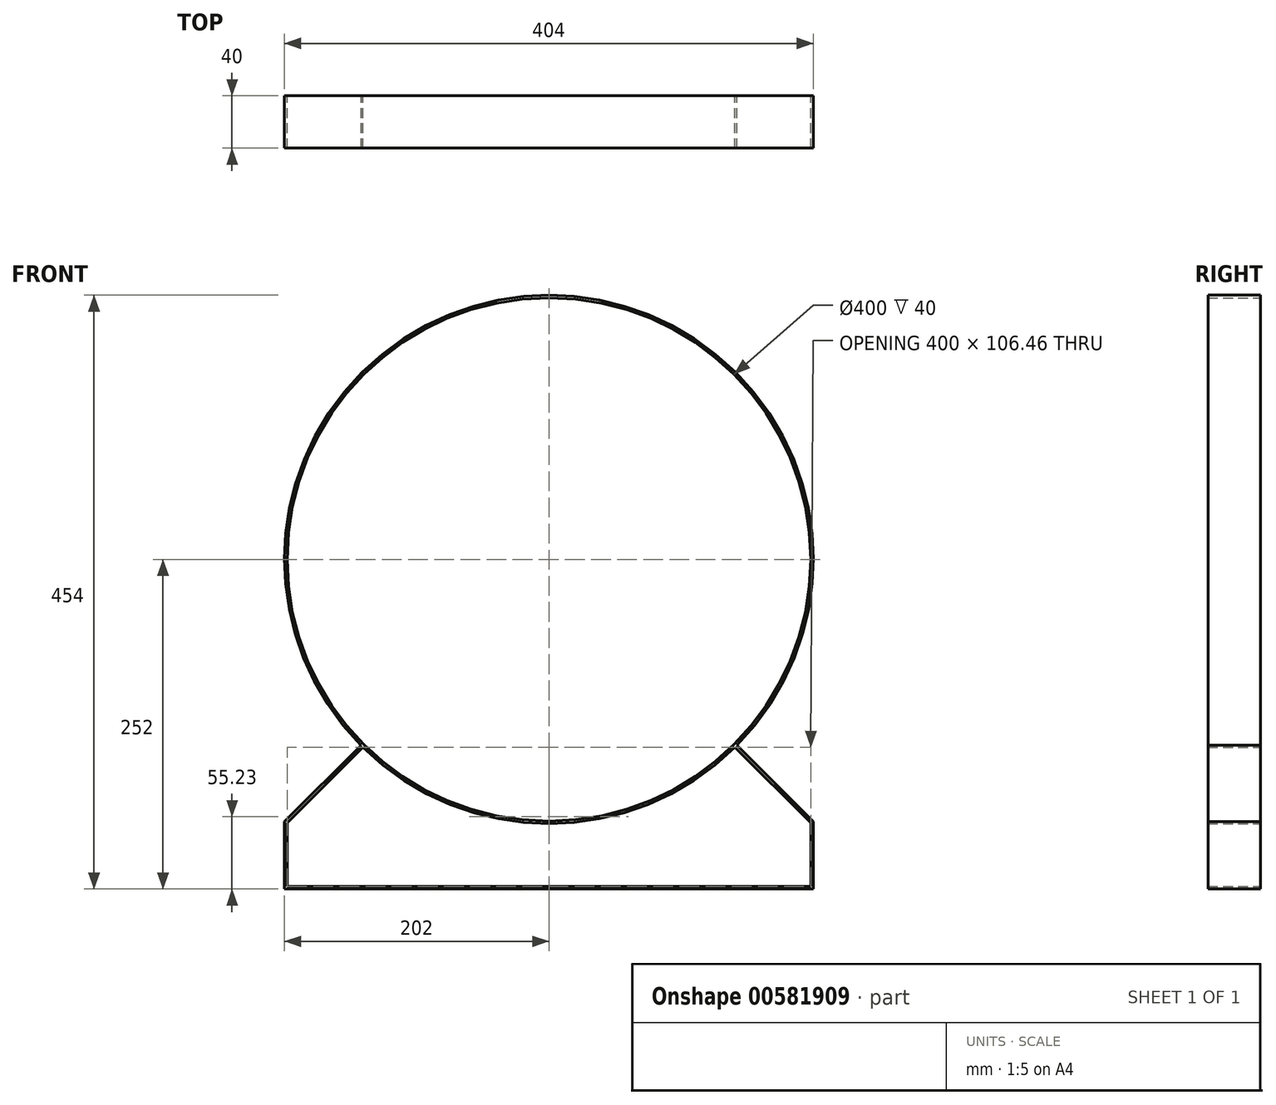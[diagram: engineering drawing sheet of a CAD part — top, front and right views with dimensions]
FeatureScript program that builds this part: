
annotation { "Feature Type Name" : "Feature", "Feature Type Description" : "" }
export const myFeature = defineFeature(function(context is Context, id is Id, definition is map)
    precondition{}
    {
        {
            var Q0;
            Q0=qCreatedBy(makeId("Front.planeOp"),FACE);
            var sketch = newSketch(context, id + "F0", { "sketchPlane" : qUnion([Q0])});
            skLineSegment(sketch, "E0", {"start": v(0, 0) * mm, "end": v(-679.96, 0) * mm, "construction": true});
            skLineSegment(sketch, "E1", {"start": v(0, 0) * mm, "end": v(0, 658.78) * mm, "construction": true});
            skLineSegment(sketch, "E2", {"start": v(0, 0) * mm, "end": v(-291.77, -291.77) * mm, "construction": true});
            skLineSegment(sketch, "E3", {"start": v(0, 0) * mm, "end": v(291.77, -291.77) * mm, "construction": true});
            skCircle(sketch, "E4", {"center": v(0, 0) * mm, "radius": 200 * mm});
            skCircle(sketch, "E5", {"center": v(0, 0) * mm, "radius": 202 * mm});
            skLineSegment(sketch, "E6", {"start": v(-202, -252) * mm, "end": v(0, -252) * mm});
            skLineSegment(sketch, "E7", {"start": v(-200, -250) * mm, "end": v(0, -250) * mm});
            skLineSegment(sketch, "E8", {"start": v(0, 0) * mm, "end": v(0, -311.11) * mm, "construction": true});
            skLineSegment(sketch, "E9", {"start": v(-200, -250) * mm, "end": v(-200, -201.41) * mm});
            skLineSegment(sketch, "E10", {"start": v(-202, -252) * mm, "end": v(-202, -200.59) * mm});
            skLineSegment(sketch, "E11", {"start": v(-143.54, -142.13) * mm, "end": v(-202, -200.59) * mm});
            skLineSegment(sketch, "E12", {"start": v(-142.13, -143.54) * mm, "end": v(-200, -201.41) * mm});
            skLineSegment(sketch, "E13.MirrorCS", {"start": v(142.13, -143.54) * mm, "end": v(200, -201.41) * mm});
            skLineSegment(sketch, "E14.MirrorCS", {"start": v(202, -252) * mm, "end": v(0, -252) * mm});
            skLineSegment(sketch, "E15.MirrorCS", {"start": v(200, -250) * mm, "end": v(0, -250) * mm});
            skLineSegment(sketch, "E16.MirrorCS", {"start": v(143.54, -142.13) * mm, "end": v(202, -200.59) * mm});
            skLineSegment(sketch, "E17.MirrorCS", {"start": v(200, -250) * mm, "end": v(200, -201.41) * mm});
            skLineSegment(sketch, "E18.MirrorCS", {"start": v(202, -252) * mm, "end": v(202, -200.59) * mm});
            skSolve(sketch);
        }
        {
            var Q0;
            Q0=qSketchRegion(id+"F0",true);
            extrude(context, id + "F1", {"entities" : qUnion([Q0]), "offsetDistance" : 25 * mm, "depth" : 40 * mm});
        }
    });
